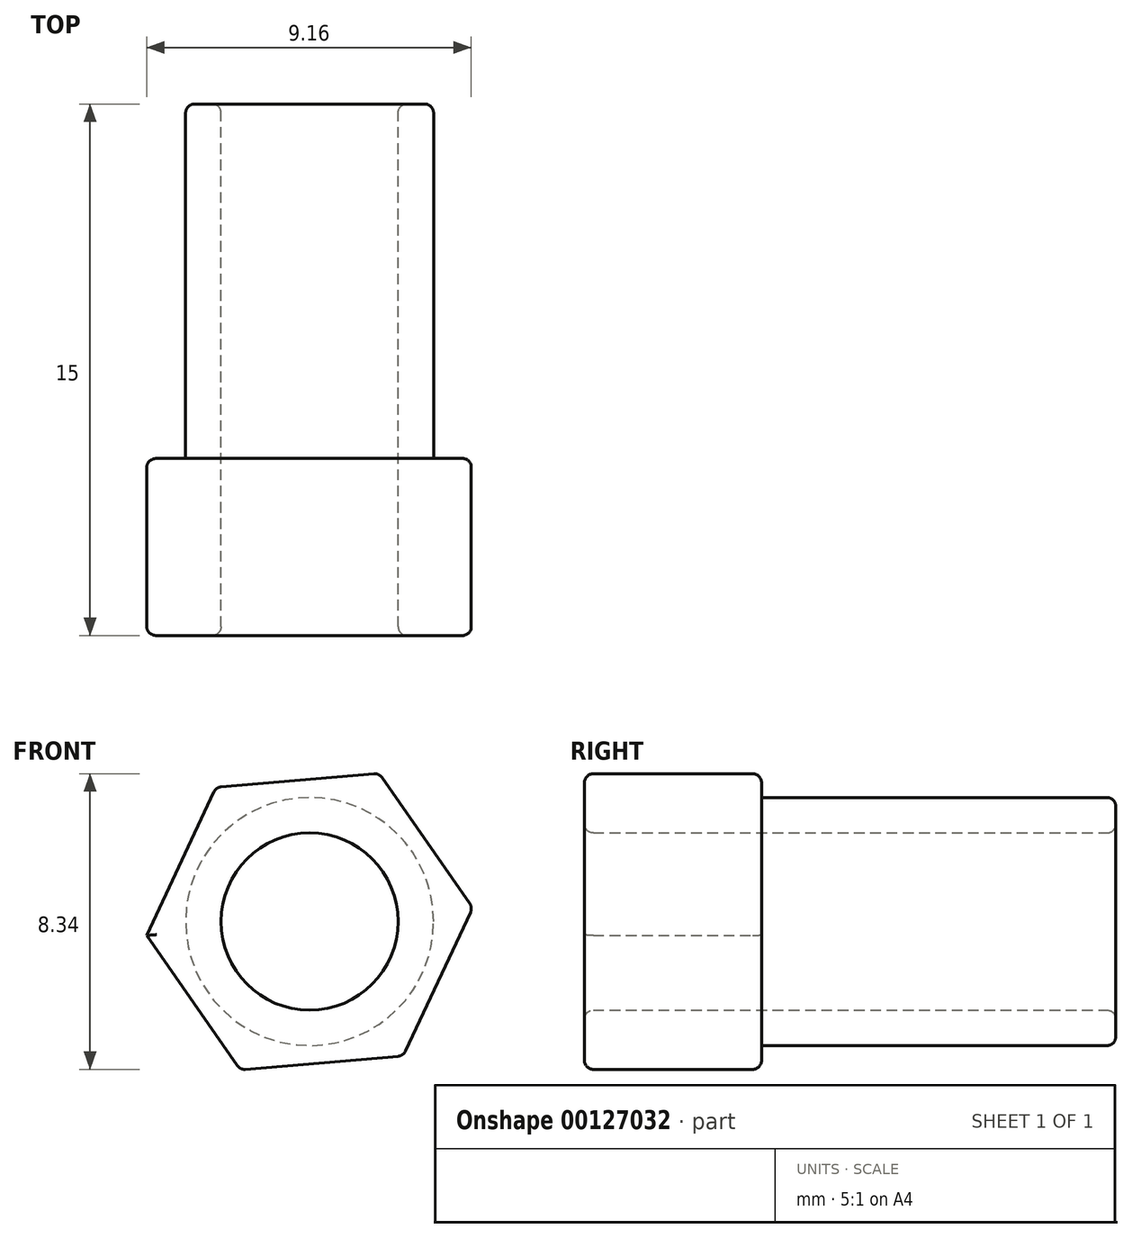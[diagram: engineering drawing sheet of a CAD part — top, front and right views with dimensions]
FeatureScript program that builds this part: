
annotation { "Feature Type Name" : "Feature", "Feature Type Description" : "" }
export const myFeature = defineFeature(function(context is Context, id is Id, definition is map)
    precondition{}
    {
        {
            var Q0;
            Q0=qCreatedBy(makeId("Front.planeOp"),FACE);
            var sketch = newSketch(context, id + "F0", { "sketchPlane" : qUnion([Q0])});
            skCircle(sketch, "E0", {"center": v(0, 0) * mm, "radius": 3.5 * mm});
            skCircle(sketch, "E1.cCircle", {"center": v(0, 0) * mm, "radius": 4 * mm, "construction": true});
            skLineSegment(sketch, "E1.0", {"start": v(4.6, 0.4) * mm, "end": v(2.64, -3.79) * mm});
            skLineSegment(sketch, "E1.1", {"start": v(2.64, -3.79) * mm, "end": v(-1.96, -4.18) * mm});
            skLineSegment(sketch, "E1.2", {"start": v(-1.96, -4.18) * mm, "end": v(-4.6, -0.4) * mm});
            skLineSegment(sketch, "E1.3", {"start": v(-4.6, -0.4) * mm, "end": v(-2.64, 3.79) * mm});
            skLineSegment(sketch, "E1.4", {"start": v(-2.64, 3.79) * mm, "end": v(1.96, 4.18) * mm});
            skLineSegment(sketch, "E1.5", {"start": v(1.96, 4.18) * mm, "end": v(4.6, 0.4) * mm});
            skPoint(sketch, "E1.0.midPoint", {"position": v(3.62, -1.7) * mm});
            skCircle(sketch, "E2", {"center": v(0, 0) * mm, "radius": 2.5 * mm});
            skSolve(sketch);
        }
        {
            var Q0;
            Q0=makeQuery(id+"F0.imprint","IMPRINT",FACE,{"disambiguationData":[TD([[makeQuery(id+"F0.imprint","IMPRINT",EDGE,{"derivedFrom":sQuery(id+"F0.wireOp",EDGE,"E0")}),1.0]])]});
            extrude(context, id + "F1", {"entities" : qUnion([Q0]), "depth" : 10 * mm});
        }
        {
            var Q0;
            Q0=makeQuery(id+"F0.imprint","IMPRINT",FACE,{"disambiguationData":[TD([[makeQuery(id+"F0.imprint","IMPRINT",EDGE,{"derivedFrom":sQuery(id+"F0.wireOp",EDGE,"E0")}),-1.0]])]});
            var Q1;
            Q1=makeQuery(id+"F0.imprint","IMPRINT",FACE,{"disambiguationData":[TD([[makeQuery(id+"F0.imprint","IMPRINT",EDGE,{"derivedFrom":sQuery(id+"F0.wireOp",EDGE,"E0")}),1.0]])]});
            extrude(context, id + "F2", {"entities" : qUnion([Q0, Q1]), "operationType" : NewBodyOperationType.ADD, "depth" : 15 * mm, "hasSecondDirection" : true, "secondDirectionOppositeDirection" : false, "secondDirectionDepth" : 10 * mm});
        }
        {
            var Q0;
            Q0=makeQuery(id+"F2.opExtrude","CAP_EDGE",EDGE,{"disambiguationData":[OSD([sQuery(id+"F0.wireOp",EDGE,"E2")])],"isStart":false});
            var Q1;
            Q1=makeQuery(id+"F2.opExtrude","CAP_EDGE",EDGE,{"disambiguationData":[OSD([sQuery(id+"F0.wireOp",EDGE,"E1.4")])],"isStart":false});
            var Q2;
            Q2=makeQuery(id+"F2.opExtrude","CAP_EDGE",EDGE,{"disambiguationData":[OSD([sQuery(id+"F0.wireOp",EDGE,"E1.4")])],"isStart":true});
            var Q3;
            Q3=makeQuery(id+"F2.opExtrude","SWEPT_EDGE",EDGE,{"disambiguationData":[OSD([sQuery(id+"F0.wireOp",EDGE,"E1.4"),sQuery(id+"F0.wireOp",EDGE,"E1.5")])]});
            var Q4;
            Q4=makeQuery(id+"F1.opExtrude","CAP_EDGE",EDGE,{"disambiguationData":[OSD([sQuery(id+"F0.wireOp",EDGE,"E0")])],"isStart":true});
            var Q5;
            Q5=makeQuery(id+"F2.opExtrude","SWEPT_EDGE",EDGE,{"disambiguationData":[OSD([sQuery(id+"F0.wireOp",EDGE,"E1.3"),sQuery(id+"F0.wireOp",EDGE,"E1.4")])]});
            var Q6;
            Q6=makeQuery(id+"F2.opExtrude","CAP_EDGE",EDGE,{"disambiguationData":[OSD([sQuery(id+"F0.wireOp",EDGE,"E1.3")])],"isStart":false});
            var Q7;
            Q7=makeQuery(id+"F2.opExtrude","CAP_EDGE",EDGE,{"disambiguationData":[OSD([sQuery(id+"F0.wireOp",EDGE,"E1.2")])],"isStart":false});
            var Q8;
            Q8=makeQuery(id+"F2.opExtrude","CAP_EDGE",EDGE,{"disambiguationData":[OSD([sQuery(id+"F0.wireOp",EDGE,"E1.3")])],"isStart":true});
            var Q9;
            Q9=makeQuery(id+"F2.opExtrude","CAP_EDGE",EDGE,{"disambiguationData":[OSD([sQuery(id+"F0.wireOp",EDGE,"E1.2")])],"isStart":true});
            var Q10;
            Q10=makeQuery(id+"F2.opExtrude","SWEPT_EDGE",EDGE,{"disambiguationData":[OSD([sQuery(id+"F0.wireOp",EDGE,"E1.1"),sQuery(id+"F0.wireOp",EDGE,"E1.2")])]});
            var Q11;
            Q11=makeQuery(id+"F2.opExtrude","CAP_EDGE",EDGE,{"disambiguationData":[OSD([sQuery(id+"F0.wireOp",EDGE,"E1.1")])],"isStart":true});
            var Q12;
            Q12=makeQuery(id+"F2.opExtrude","SWEPT_EDGE",EDGE,{"disambiguationData":[OSD([sQuery(id+"F0.wireOp",EDGE,"E1.0"),sQuery(id+"F0.wireOp",EDGE,"E1.1")])]});
            var Q13;
            Q13=makeQuery(id+"F2.opExtrude","CAP_EDGE",EDGE,{"disambiguationData":[OSD([sQuery(id+"F0.wireOp",EDGE,"E1.1")])],"isStart":false});
            var Q14;
            Q14=makeQuery(id+"F2.opExtrude","CAP_EDGE",EDGE,{"disambiguationData":[OSD([sQuery(id+"F0.wireOp",EDGE,"E1.0")])],"isStart":false});
            var Q15;
            Q15=makeQuery(id+"F2.opExtrude","CAP_EDGE",EDGE,{"disambiguationData":[OSD([sQuery(id+"F0.wireOp",EDGE,"E1.5")])],"isStart":false});
            var Q16;
            Q16=makeQuery(id+"F2.opExtrude","SWEPT_EDGE",EDGE,{"disambiguationData":[OSD([sQuery(id+"F0.wireOp",EDGE,"E1.0"),sQuery(id+"F0.wireOp",EDGE,"E1.5")])]});
            var Q17;
            Q17=makeQuery(id+"F2.opExtrude","CAP_EDGE",EDGE,{"disambiguationData":[OSD([sQuery(id+"F0.wireOp",EDGE,"E1.0")])],"isStart":true});
            var Q18;
            Q18=makeQuery(id+"F2.opExtrude","CAP_EDGE",EDGE,{"disambiguationData":[OSD([sQuery(id+"F0.wireOp",EDGE,"E1.5")])],"isStart":true});
            var Q19;
            Q19=makeQuery(id+"F1.opExtrude","CAP_EDGE",EDGE,{"disambiguationData":[OSD([sQuery(id+"F0.wireOp",EDGE,"E0")])],"isStart":false});
            var Q20;
            Q20=makeQuery(id+"F1.opExtrude","CAP_EDGE",EDGE,{"disambiguationData":[OSD([sQuery(id+"F0.wireOp",EDGE,"E2")])],"isStart":true});
            fillet(context, id + "F3", {"entities" : qUnion([Q0, Q1, Q2, Q3, Q4, Q5, Q6, Q7, Q8, Q9, Q10, Q11, Q12, Q13, Q14, Q15, Q16, Q17, Q18, Q19, Q20]), "radius" : .25 * mm, "tangentPropagation" : true, "allowEdgeOverflow" : false});
        }
    });
